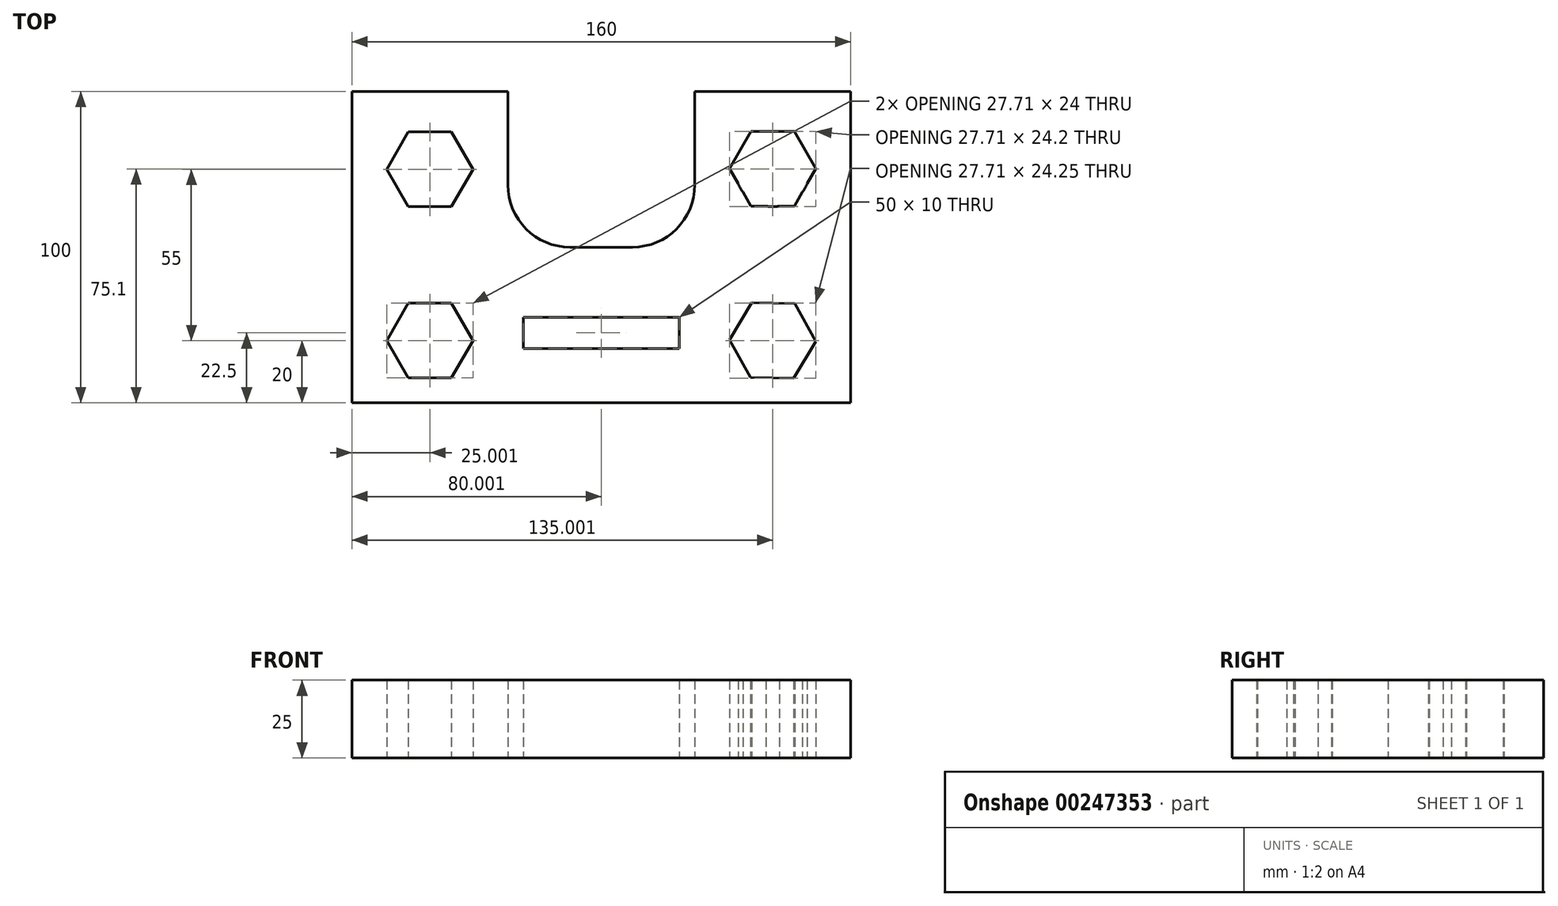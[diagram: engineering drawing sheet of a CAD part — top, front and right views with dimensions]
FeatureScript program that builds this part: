
annotation { "Feature Type Name" : "Feature", "Feature Type Description" : "" }
export const myFeature = defineFeature(function(context is Context, id is Id, definition is map)
    precondition{}
    {
        {
            var Q0;
            Q0=qCreatedBy(makeId("Top.planeOp"),FACE);
            var sketch = newSketch(context, id + "F0", { "sketchPlane" : qUnion([Q0])});
            skLineSegment(sketch, "E0", {"start": v(-70.64, -87) * mm, "end": v(89.36, -87) * mm});
            skLineSegment(sketch, "E1", {"start": v(89.36, -87) * mm, "end": v(89.36, 13) * mm});
            skLineSegment(sketch, "E2", {"start": v(89.36, 13) * mm, "end": v(39.36, 13) * mm});
            skLineSegment(sketch, "E3", {"start": v(39.36, 13) * mm, "end": v(39.36, -17) * mm});
            skLineSegment(sketch, "E4", {"start": v(19.36, -37) * mm, "end": v(-0.64, -37) * mm});
            skLineSegment(sketch, "E5", {"start": v(-20.64, -17) * mm, "end": v(-20.64, 13) * mm});
            skLineSegment(sketch, "E6", {"start": v(-20.64, 13) * mm, "end": v(-70.64, 13) * mm});
            skLineSegment(sketch, "E7", {"start": v(-70.64, 13) * mm, "end": v(-70.64, -87) * mm});
            skPoint(sketch, "E8.visualSharp", {"position": v(-20.64, -37) * mm});
            skArc(sketch, "E8.filletArc", {"start": v(-20.64, -17) * mm, "mid": v(-14.78, -31.14) * mm, "end": v(-0.64, -37) * mm});
            skPoint(sketch, "E9.visualSharp", {"position": v(39.36, -37) * mm});
            skArc(sketch, "E9.filletArc", {"start": v(19.36, -37) * mm, "mid": v(33.5, -31.14) * mm, "end": v(39.36, -17) * mm});
            skLineSegment(sketch, "E10", {"start": v(89.36, -87) * mm, "end": v(64.36, -87) * mm});
            skLineSegment(sketch, "E11", {"start": v(64.36, -87) * mm, "end": v(64.36, -67) * mm});
            skLineSegment(sketch, "E12", {"start": v(64.36, -67) * mm, "end": v(64.36, -12) * mm});
            skLineSegment(sketch, "E13", {"start": v(-70.64, -87) * mm, "end": v(-45.64, -87) * mm});
            skLineSegment(sketch, "E14", {"start": v(-45.64, -87) * mm, "end": v(-45.64, -67) * mm});
            skLineSegment(sketch, "E15", {"start": v(-45.64, -67) * mm, "end": v(-45.64, -12) * mm});
            skLineSegment(sketch, "E16.0", {"start": v(71.29, 0.2) * mm, "end": v(78.22, -11.8) * mm});
            skLineSegment(sketch, "E16.1", {"start": v(78.22, -11.8) * mm, "end": v(71.29, -23.8) * mm});
            skLineSegment(sketch, "E16.2", {"start": v(71.29, -23.8) * mm, "end": v(57.43, -23.8) * mm});
            skLineSegment(sketch, "E16.3", {"start": v(57.43, -23.8) * mm, "end": v(50.5, -11.8) * mm});
            skLineSegment(sketch, "E16.4", {"start": v(50.5, -11.8) * mm, "end": v(57.43, 0.2) * mm});
            skLineSegment(sketch, "E16.5", {"start": v(57.43, 0.2) * mm, "end": v(71.29, 0.2) * mm});
            skPoint(sketch, "E16.0.midPoint", {"position": v(74.75, -5.8) * mm});
            skCircle(sketch, "E17", {"center": v(64.36, -12) * mm, "radius": 12 * mm});
            skLineSegment(sketch, "E18.0", {"start": v(71.5, -55.13) * mm, "end": v(78.21, -67.25) * mm});
            skLineSegment(sketch, "E18.1", {"start": v(78.21, -67.25) * mm, "end": v(71.07, -79.12) * mm});
            skLineSegment(sketch, "E18.2", {"start": v(71.07, -79.12) * mm, "end": v(57.22, -78.87) * mm});
            skLineSegment(sketch, "E18.3", {"start": v(57.22, -78.87) * mm, "end": v(50.5, -66.75) * mm});
            skLineSegment(sketch, "E18.4", {"start": v(50.5, -66.75) * mm, "end": v(57.65, -54.88) * mm});
            skLineSegment(sketch, "E18.5", {"start": v(57.65, -54.88) * mm, "end": v(71.5, -55.13) * mm});
            skPoint(sketch, "E18.0.midPoint", {"position": v(74.86, -61.19) * mm});
            skLineSegment(sketch, "E19.0", {"start": v(-52.57, 0) * mm, "end": v(-38.71, 0) * mm});
            skLineSegment(sketch, "E19.1", {"start": v(-38.71, 0) * mm, "end": v(-31.78, -12) * mm});
            skLineSegment(sketch, "E19.2", {"start": v(-31.78, -12) * mm, "end": v(-38.71, -24) * mm});
            skLineSegment(sketch, "E19.3", {"start": v(-38.71, -24) * mm, "end": v(-52.57, -24) * mm});
            skLineSegment(sketch, "E19.4", {"start": v(-52.57, -24) * mm, "end": v(-59.5, -12) * mm});
            skLineSegment(sketch, "E19.5", {"start": v(-59.5, -12) * mm, "end": v(-52.57, 0) * mm});
            skPoint(sketch, "E19.0.midPoint", {"position": v(-45.64, 0) * mm});
            skLineSegment(sketch, "E20.0", {"start": v(-52.57, -55) * mm, "end": v(-38.71, -55) * mm});
            skLineSegment(sketch, "E20.1", {"start": v(-38.71, -55) * mm, "end": v(-31.78, -67) * mm});
            skLineSegment(sketch, "E20.2", {"start": v(-31.78, -67) * mm, "end": v(-38.71, -79) * mm});
            skLineSegment(sketch, "E20.3", {"start": v(-38.71, -79) * mm, "end": v(-52.57, -79) * mm});
            skLineSegment(sketch, "E20.4", {"start": v(-52.57, -79) * mm, "end": v(-59.5, -67) * mm});
            skLineSegment(sketch, "E20.5", {"start": v(-59.5, -67) * mm, "end": v(-52.57, -55) * mm});
            skPoint(sketch, "E20.0.midPoint", {"position": v(-45.64, -55) * mm});
            skCircle(sketch, "E21", {"center": v(-45.64, -12) * mm, "radius": 12 * mm});
            skCircle(sketch, "E22", {"center": v(-45.64, -67) * mm, "radius": 12 * mm});
            skCircle(sketch, "E23", {"center": v(64.36, -67) * mm, "radius": 12 * mm});
            skLineSegment(sketch, "E24", {"start": v(-70.64, -87) * mm, "end": v(-15.64, -87) * mm});
            skLineSegment(sketch, "E25", {"start": v(-15.64, -87) * mm, "end": v(-70.64, -87) * mm});
            skLineSegment(sketch, "E26", {"start": v(-15.64, -87) * mm, "end": v(34.36, -87) * mm});
            skLineSegment(sketch, "E27", {"start": v(34.36, -69.5) * mm, "end": v(-15.64, -69.5) * mm});
            skLineSegment(sketch, "E28", {"start": v(-15.64, -59.5) * mm, "end": v(34.36, -59.5) * mm});
            skLineSegment(sketch, "E29", {"start": v(-15.64, -59.5) * mm, "end": v(-15.64, -69.5) * mm});
            skLineSegment(sketch, "E30", {"start": v(34.36, -59.5) * mm, "end": v(34.36, -69.5) * mm});
            skLineSegment(sketch, "E31", {"start": v(34.36, -64.5) * mm, "end": v(34.36, -87) * mm});
            skSolve(sketch);
        }
        {
            var Q0;
            Q0 = qSketchRegion(id + "F0", true);
            extrude(context, id + "F1", {"entities" : qUnion([Q0]), "depth" : 25 * mm});
        }
    });
